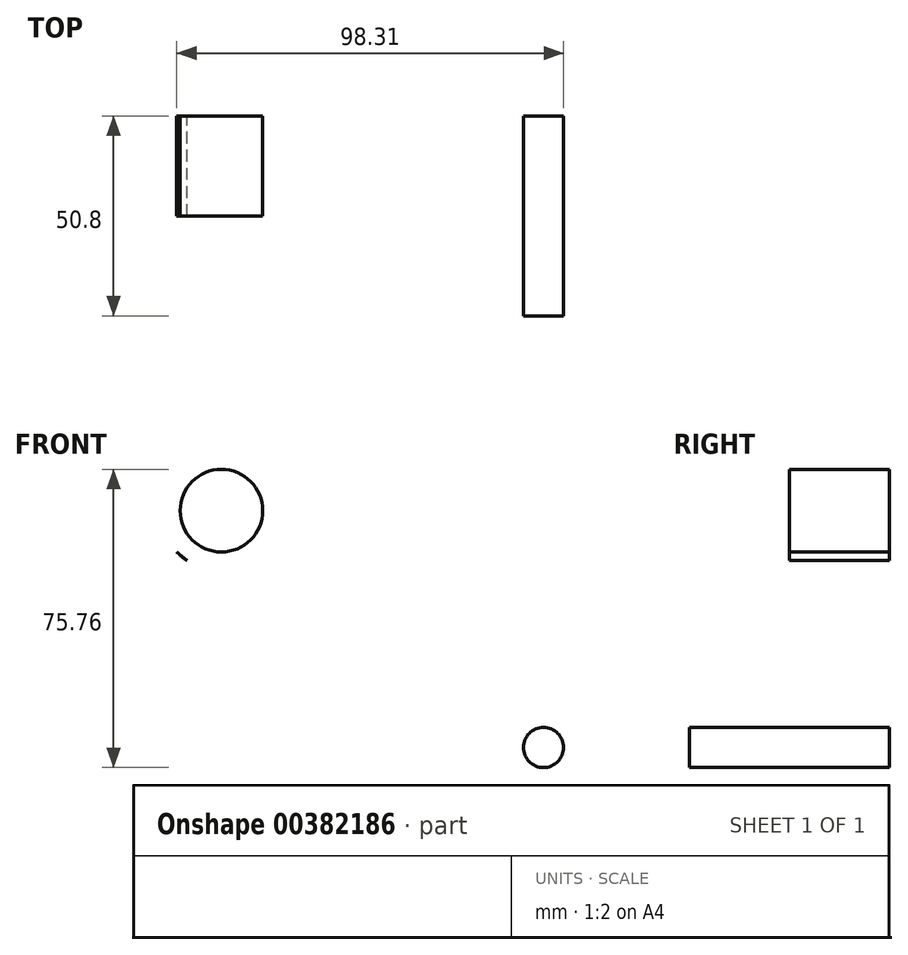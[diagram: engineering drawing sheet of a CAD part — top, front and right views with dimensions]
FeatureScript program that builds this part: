
annotation { "Feature Type Name" : "Feature", "Feature Type Description" : "" }
export const myFeature = defineFeature(function(context is Context, id is Id, definition is map)
    precondition{}
    {
        {
            var Q0;
            Q0=qCreatedBy(makeId("Front.planeOp"),FACE);
            var sketch = newSketch(context, id + "F0", { "sketchPlane" : qUnion([Q0])});
            skCircle(sketch, "E0", {"center": v(33.39, 0) * mm, "radius": 25.84 * mm});
            skCircle(sketch, "E1", {"center": v(-50.23, 59.56) * mm, "radius": 14.37 * mm});
            skLineSegment(sketch, "E2", {"start": v(-60.7, 49.73) * mm, "end": v(9.2, -9.08) * mm});
            skSolve(sketch);
        }
        {
            var Q0;
            {var subQ0=sQuery(id+"F0.wireOp",EDGE,"E2");var subQ1=sQuery(id+"F0.wireOp",EDGE,"E1");var subQ2=makeQuery(id+"F0.imprint","INTERSECT",VERTEX,{"disambiguationData":[OD(0.0)],"derivedFrom":[subQ1,subQ0]});Q0=makeQuery(id+"F0.imprint","IMPRINT",FACE,{"disambiguationData":[TD([[makeQuery(id+"F0.imprint","IMPRINT",EDGE,{"disambiguationData":[TD([[subQ2,1.0]])],"derivedFrom":subQ1}),1.0]])]});}
            var sketch = newSketch(context, id + "F1", { "sketchPlane" : qUnion([Q0])});
            skLineSegment(sketch, "E3", {"start": v(-41.8, 71.59) * mm, "end": v(45.12, 23.16) * mm});
            skCircle(sketch, "E4", {"center": v(32.49, 0) * mm, "radius": 5.11 * mm});
            skCircle(sketch, "E5", {"center": v(-49.33, 60.16) * mm, "radius": 10.5 * mm});
            skSolve(sketch);
        }
        {
            var Q0;
            Q0 = qSketchRegion(id + "F1", true);
            var Q1;
            {var subQ0=sQuery(id+"F0.wireOp",EDGE,"E2");var subQ1=sQuery(id+"F0.wireOp",EDGE,"E1");var subQ2=makeQuery(id+"F0.imprint","INTERSECT",VERTEX,{"disambiguationData":[OD(0.0)],"derivedFrom":[subQ1,subQ0]});Q1=makeQuery(id+"F0.imprint","IMPRINT",FACE,{"disambiguationData":[TD([[makeQuery(id+"F0.imprint","IMPRINT",EDGE,{"disambiguationData":[TD([[subQ2,1.0]])],"derivedFrom":subQ1}),1.0]])]});}
            extrude(context, id + "F2", {"entities" : qUnion([Q0, Q1]), "depth" : 25.4 * mm});
        }
        {
            var Q0;
            Q0=makeQuery(id+"F2.opExtrude","CAP_FACE",FACE,{"disambiguationData":[OSD([sQuery(id+"F1.wireOp",EDGE,"E4")])],"isStart":false});
            var Q1;
            Q1=makeQuery(id+"F2.opExtrude","CAP_FACE",FACE,{"disambiguationData":[OSD([sQuery(id+"F1.wireOp",EDGE,"E4")])],"isStart":true});
            extrude(context, id + "F3", {"entities" : qUnion([Q0, Q1]), "operationType" : NewBodyOperationType.ADD, "depth" : 25.4 * mm});
        }
    });
